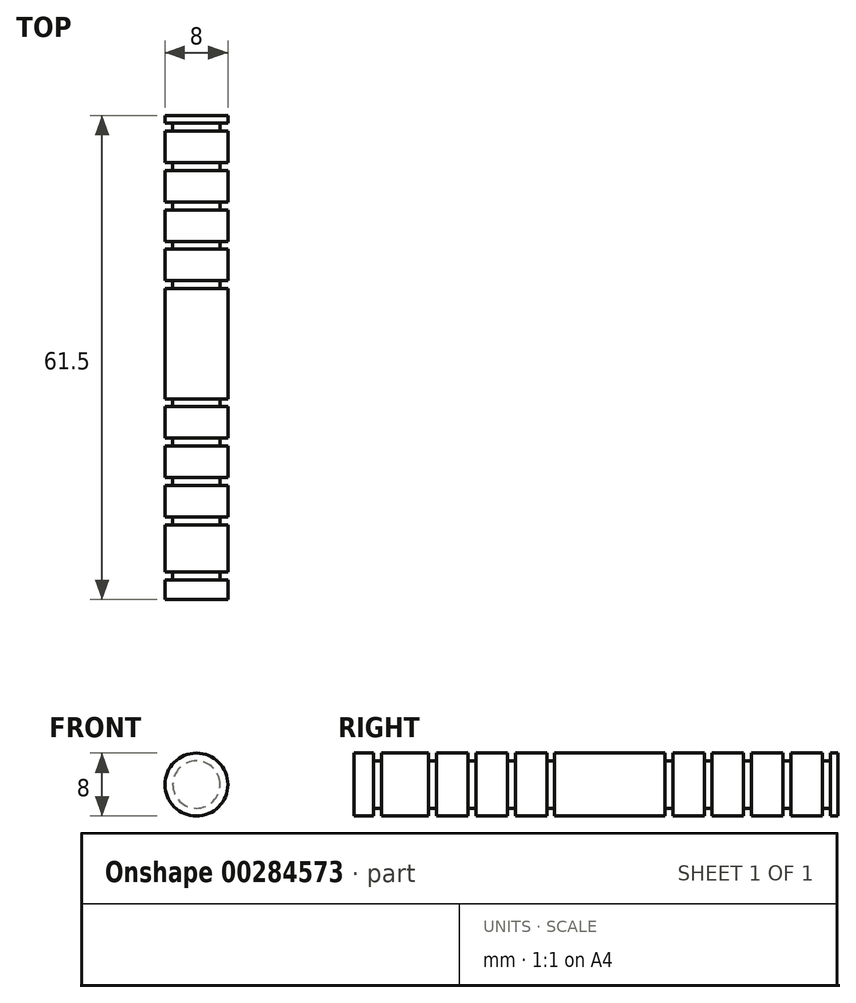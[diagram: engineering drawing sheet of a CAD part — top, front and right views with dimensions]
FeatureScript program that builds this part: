
annotation { "Feature Type Name" : "Feature", "Feature Type Description" : "" }
export const myFeature = defineFeature(function(context is Context, id is Id, definition is map)
    precondition{}
    {
        {
            var Q0;
            Q0=qCreatedBy(makeId("Right.planeOp"),FACE);
            var sketch = newSketch(context, id + "F0", { "sketchPlane" : qUnion([Q0])});
            skLineSegment(sketch, "E0", {"start": v(0, 0) * mm, "end": v(0, 4) * mm});
            skLineSegment(sketch, "E1", {"start": v(0, 4) * mm, "end": v(2.5, 4) * mm});
            skLineSegment(sketch, "E2", {"start": v(61.5, 4) * mm, "end": v(61.5, 0) * mm});
            skLineSegment(sketch, "E3", {"start": v(61.5, 0) * mm, "end": v(0, 0) * mm});
            skLineSegment(sketch, "E4", {"start": v(2.5, 4) * mm, "end": v(2.5, 3) * mm});
            skLineSegment(sketch, "E5", {"start": v(2.5, 3) * mm, "end": v(3.5, 3) * mm});
            skLineSegment(sketch, "E6", {"start": v(3.5, 3) * mm, "end": v(3.5, 4) * mm});
            skLineSegment(sketch, "E7", {"start": v(59.5, 4) * mm, "end": v(59.5, 3) * mm});
            skLineSegment(sketch, "E8", {"start": v(59.5, 3) * mm, "end": v(60.5, 3) * mm});
            skLineSegment(sketch, "E9", {"start": v(60.5, 3) * mm, "end": v(60.5, 4) * mm});
            skLineSegment(sketch, "E10.trimOffspring", {"start": v(3.5, 4) * mm, "end": v(9.5, 4) * mm});
            skLineSegment(sketch, "E11.trimOffspring", {"start": v(60.5, 4) * mm, "end": v(61.5, 4) * mm});
            skPoint(sketch, "E12.oppositeSnap0", {"position": v(61.5, 2) * mm});
            skLineSegment(sketch, "E12.top", {"start": v(44.5, 3) * mm, "end": v(45.5, 3) * mm});
            skLineSegment(sketch, "E12.left", {"start": v(44.5, 4) * mm, "end": v(44.5, 3) * mm});
            skLineSegment(sketch, "E12.right", {"start": v(45.5, 4) * mm, "end": v(45.5, 3) * mm});
            skLineSegment(sketch, "E13.top", {"start": v(39.5, 3) * mm, "end": v(40.5, 3) * mm});
            skLineSegment(sketch, "E13.left", {"start": v(39.5, 4) * mm, "end": v(39.5, 3) * mm});
            skLineSegment(sketch, "E13.right", {"start": v(40.5, 4) * mm, "end": v(40.5, 3) * mm});
            skLineSegment(sketch, "E14.trimOffspring", {"start": v(40.5, 4) * mm, "end": v(44.5, 4) * mm});
            skLineSegment(sketch, "E15.trimOffspring", {"start": v(45.5, 4) * mm, "end": v(49.5, 4) * mm});
            skLineSegment(sketch, "E16.top", {"start": v(49.5, 3) * mm, "end": v(50.5, 3) * mm});
            skLineSegment(sketch, "E16.left", {"start": v(49.5, 4) * mm, "end": v(49.5, 3) * mm});
            skLineSegment(sketch, "E16.right", {"start": v(50.5, 4) * mm, "end": v(50.5, 3) * mm});
            skLineSegment(sketch, "E17.top", {"start": v(54.5, 3) * mm, "end": v(55.5, 3) * mm});
            skLineSegment(sketch, "E17.left", {"start": v(55.5, 4) * mm, "end": v(55.5, 3) * mm});
            skLineSegment(sketch, "E17.right", {"start": v(54.5, 4) * mm, "end": v(54.5, 3) * mm});
            skLineSegment(sketch, "E18.top", {"start": v(9.5, 3) * mm, "end": v(10.5, 3) * mm});
            skLineSegment(sketch, "E18.left", {"start": v(9.5, 4) * mm, "end": v(9.5, 3) * mm});
            skLineSegment(sketch, "E18.right", {"start": v(10.5, 4) * mm, "end": v(10.5, 3) * mm});
            skLineSegment(sketch, "E19.top", {"start": v(14.5, 3) * mm, "end": v(15.5, 3) * mm});
            skLineSegment(sketch, "E19.left", {"start": v(14.5, 4) * mm, "end": v(14.5, 3) * mm});
            skLineSegment(sketch, "E19.right", {"start": v(15.5, 4) * mm, "end": v(15.5, 3) * mm});
            skLineSegment(sketch, "E20.top", {"start": v(19.5, 3) * mm, "end": v(20.5, 3) * mm});
            skLineSegment(sketch, "E20.left", {"start": v(19.5, 4) * mm, "end": v(19.5, 3) * mm});
            skLineSegment(sketch, "E20.right", {"start": v(20.5, 4) * mm, "end": v(20.5, 3) * mm});
            skLineSegment(sketch, "E21.top", {"start": v(24.5, 3) * mm, "end": v(25.5, 3) * mm});
            skLineSegment(sketch, "E21.left", {"start": v(24.5, 4) * mm, "end": v(24.5, 3) * mm});
            skLineSegment(sketch, "E21.right", {"start": v(25.5, 4) * mm, "end": v(25.5, 3) * mm});
            skLineSegment(sketch, "E22.trimOffspring", {"start": v(10.5, 4) * mm, "end": v(14.5, 4) * mm});
            skLineSegment(sketch, "E23.trimOffspring", {"start": v(15.5, 4) * mm, "end": v(19.5, 4) * mm});
            skLineSegment(sketch, "E24.trimOffspring", {"start": v(20.5, 4) * mm, "end": v(24.5, 4) * mm});
            skLineSegment(sketch, "E25.trimOffspring", {"start": v(25.5, 4) * mm, "end": v(39.5, 4) * mm});
            skLineSegment(sketch, "E26.trimOffspring", {"start": v(50.5, 4) * mm, "end": v(54.5, 4) * mm});
            skLineSegment(sketch, "E27.trimOffspring", {"start": v(55.5, 4) * mm, "end": v(59.5, 4) * mm});
            skSolve(sketch);
        }
        {
            var Q0;
            Q0=qCreatedBy(makeId("Right.planeOp"),FACE);
            var sketch = newSketch(context, id + "F1", { "sketchPlane" : qUnion([Q0])});
            skLineSegment(sketch, "E28", {"start": v(-40.56, 0) * mm, "end": v(76.1, 0) * mm});
            skSolve(sketch);
        }
        {
            var Q0;
            Q0=qSketchRegion(id+"F0",true);
            var Q1;
            Q1=sQuery(id+"F1.wireOp",EDGE,"E28");
            revolve(context, id + "F2", {"entities" : qUnion([Q0]), "axis" : qUnion([Q1]), "revolveType" : RevolveType.FULL});
        }
    });
